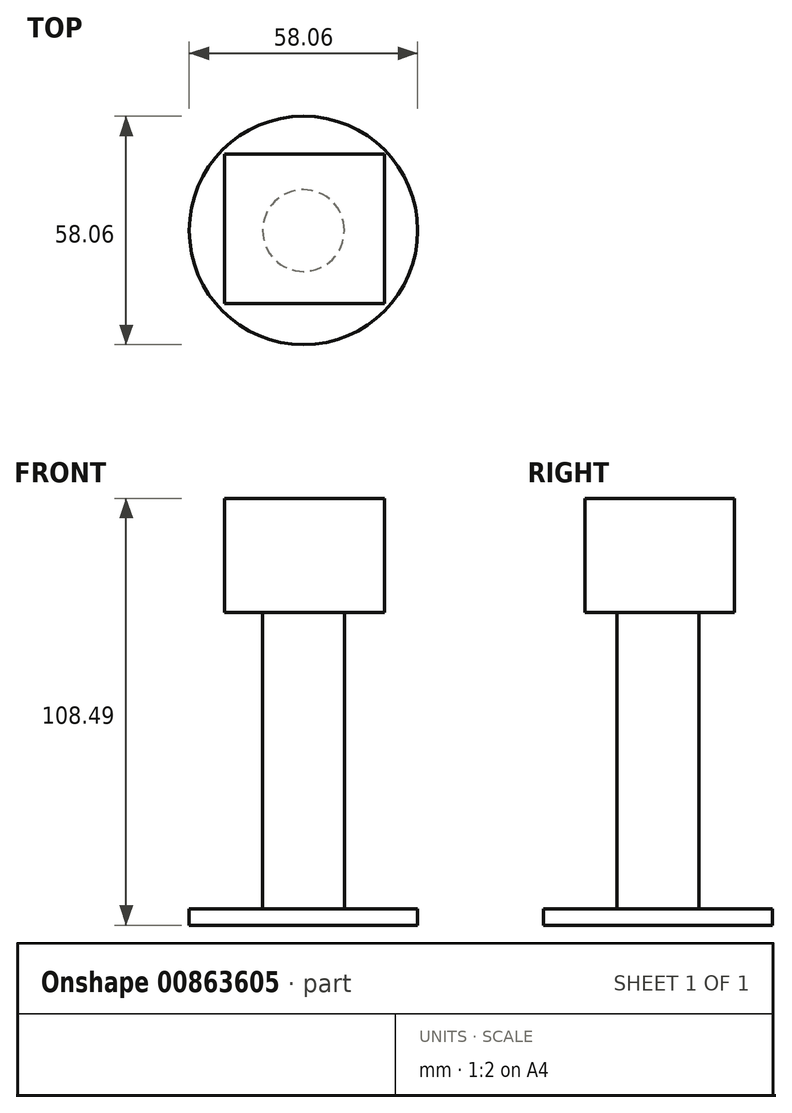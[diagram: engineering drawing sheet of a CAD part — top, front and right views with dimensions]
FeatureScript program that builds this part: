
annotation { "Feature Type Name" : "Feature", "Feature Type Description" : "" }
export const myFeature = defineFeature(function(context is Context, id is Id, definition is map)
    precondition{}
    {
        {
            var Q0;
            Q0=qCreatedBy(makeId("Front.planeOp"),FACE);
            var sketch = newSketch(context, id + "F0", { "sketchPlane" : qUnion([Q0])});
            skLineSegment(sketch, "E0.bottom", {"start": v(0, -46.77) * mm, "end": v(-29.03, -46.77) * mm});
            skLineSegment(sketch, "E0.top", {"start": v(0, -42.56) * mm, "end": v(-29.03, -42.56) * mm});
            skLineSegment(sketch, "E0.left", {"start": v(0, -46.77) * mm, "end": v(0, -42.56) * mm});
            skLineSegment(sketch, "E0.right", {"start": v(-29.03, -46.77) * mm, "end": v(-29.03, -42.56) * mm});
            skLineSegment(sketch, "E1", {"start": v(-10.38, -42.56) * mm, "end": v(-10.38, 35.64) * mm});
            skLineSegment(sketch, "E2", {"start": v(-10.38, 35.64) * mm, "end": v(0, 35.64) * mm});
            skLineSegment(sketch, "E3", {"start": v(0, 35.64) * mm, "end": v(0, -42.56) * mm});
            skSolve(sketch);
        }
        {
            var Q0;
            {var subQ2=sQuery(id+"F0.wireOp",EDGE,"E1");Q0=makeQuery(id+"F0.imprint","IMPRINT",FACE,{"disambiguationData":[TD([[makeQuery(id+"F0.imprint","IMPRINT",EDGE,{"derivedFrom":subQ2}),-1.0]])]});}
            var Q1;
            Q1=makeQuery(id+"F0.imprint","IMPRINT",FACE,{"disambiguationData":[TD([[makeQuery(id+"F0.imprint","IMPRINT",EDGE,{"derivedFrom":sQuery(id+"F0.wireOp",EDGE,"E0.bottom")}),-1.0]])]});
            var Q2;
            Q2=sQuery(id+"F0.wireOp",EDGE,"E3");
            revolve(context, id + "F1", {"surfaceOperationType" : NewSurfaceOperationType.NEW, "entities" : qUnion([Q0, Q1]), "axis" : qUnion([Q2]), "revolveType" : RevolveType.FULL});
        }
        {
            var Q0;
            Q0=qCreatedBy(makeId("Top.planeOp"),FACE);
            var sketch = newSketch(context, id + "F2", { "sketchPlane" : qUnion([Q0])});
            skLineSegment(sketch, "E4", {"start": v(-20, 19.4) * mm, "end": v(20.6, 19.4) * mm});
            skLineSegment(sketch, "E5", {"start": v(20.6, 19.4) * mm, "end": v(20.6, -18.5) * mm});
            skLineSegment(sketch, "E6", {"start": v(20.6, -18.5) * mm, "end": v(-20, -18.5) * mm});
            skLineSegment(sketch, "E7", {"start": v(-20, -18.5) * mm, "end": v(-20, 19.4) * mm});
            skSolve(sketch);
        }
        {
            var Q0;
            Q0 = qSketchRegion(id + "F2", true);
            extrude(context, id + "F3", {"entities" : qUnion([Q0]), "operationType" : NewBodyOperationType.ADD, "depth" : 61.72 * mm, "offsetDistance" : 25.4 * mm, "hasSecondDirection" : true, "secondDirectionOppositeDirection" : false, "secondDirectionDepth" : 32.77 * mm});
        }
    });
